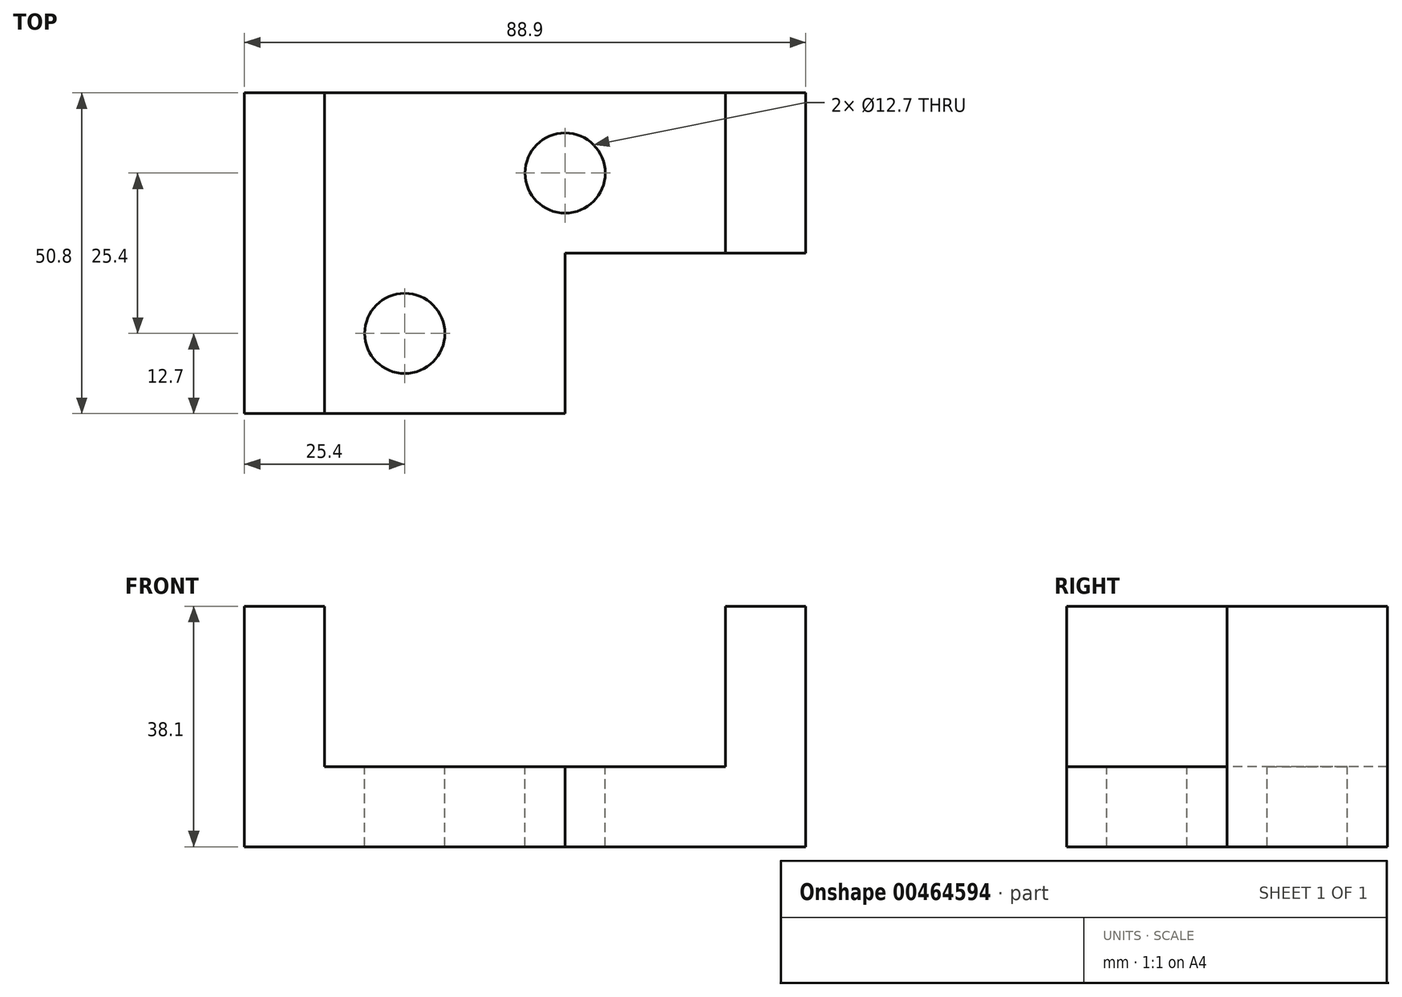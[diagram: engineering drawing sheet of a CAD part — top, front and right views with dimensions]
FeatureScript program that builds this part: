
annotation { "Feature Type Name" : "Feature", "Feature Type Description" : "" }
export const myFeature = defineFeature(function(context is Context, id is Id, definition is map)
    precondition{}
    {
        {
            var Q0;
            Q0=qCreatedBy(makeId("Front.planeOp"),FACE);
            var sketch = newSketch(context, id + "F0", { "sketchPlane" : qUnion([Q0])});
            skLineSegment(sketch, "E0.bottom", {"start": v(44.45, 19.05) * mm, "end": v(-44.45, 19.05) * mm});
            skLineSegment(sketch, "E0.top", {"start": v(44.45, -19.05) * mm, "end": v(-44.45, -19.05) * mm});
            skLineSegment(sketch, "E0.left", {"start": v(44.45, 19.05) * mm, "end": v(44.45, -19.05) * mm});
            skLineSegment(sketch, "E0.right", {"start": v(-44.45, 19.05) * mm, "end": v(-44.45, -19.05) * mm});
            skPoint(sketch, "E0.middle", {"position": v(0, 0) * mm});
            skSolve(sketch);
        }
        {
            var Q0;
            Q0=qSketchRegion(id+"F0",true);
            extrude(context, id + "F1", {"entities" : qUnion([Q0]), "depth" : 50.8 * mm});
        }
        {
            var Q0;
            Q0=makeQuery(id+"F1.opExtrude","CAP_FACE",FACE,{"disambiguationData":[OSD([sQuery(id+"F0.wireOp",EDGE,"E0.bottom"),sQuery(id+"F0.wireOp",EDGE,"E0.top"),sQuery(id+"F0.wireOp",EDGE,"E0.left"),sQuery(id+"F0.wireOp",EDGE,"E0.right")])],"isStart":false});
            var sketch = newSketch(context, id + "F2", { "sketchPlane" : qUnion([Q0])});
            skLineSegment(sketch, "E1", {"start": v(-44.45, 19.05) * mm, "end": v(-31.75, 19.05) * mm});
            skLineSegment(sketch, "E2", {"start": v(-31.75, -6.35) * mm, "end": v(-31.75, 19.05) * mm});
            skLineSegment(sketch, "E3", {"start": v(-31.75, -6.35) * mm, "end": v(31.75, -6.35) * mm});
            skLineSegment(sketch, "E4", {"start": v(31.75, -6.35) * mm, "end": v(31.75, 19.05) * mm});
            skLineSegment(sketch, "E5", {"start": v(31.75, 19.05) * mm, "end": v(44.45, 19.05) * mm});
            skSolve(sketch);
        }
        {
            var Q0;
            {var subQ0=sQuery(id+"F2.wireOp",EDGE,"E2");Q0=makeQuery(id+"F2.imprint","IMPRINT",FACE,{"disambiguationData":[TD([[makeQuery(id+"F2.imprint","IMPRINT",EDGE,{"derivedFrom":subQ0}),-1.0]])]});}
            extrude(context, id + "F3", {"entities" : qUnion([Q0]), "operationType" : NewBodyOperationType.REMOVE, "endBound" : BoundingType.THROUGH_ALL, "oppositeDirection" : true, "depth" : 25.4 * mm});
        }
        {
            var Q0;
            Q0=makeQuery(id+"F3.boolean.opBoolean","COPY",FACE,{"derivedFrom":makeQuery(id+"F3.opExtrude","SWEPT_FACE",FACE,{"disambiguationData":[OSD([sQuery(id+"F2.wireOp",EDGE,"E3")])]})});
            var sketch = newSketch(context, id + "F4", { "sketchPlane" : qUnion([Q0])});
            skPoint(sketch, "E6.startSnap0", {"position": v(6.35, -25.4) * mm});
            skLineSegment(sketch, "E7.bottom", {"start": v(6.35, -25.4) * mm, "end": v(31.75, -25.4) * mm});
            skLineSegment(sketch, "E7.top", {"start": v(6.35, -50.8) * mm, "end": v(31.75, -50.8) * mm});
            skLineSegment(sketch, "E7.left", {"start": v(6.35, -25.4) * mm, "end": v(6.35, -50.8) * mm});
            skLineSegment(sketch, "E7.right", {"start": v(31.75, -25.4) * mm, "end": v(31.75, -50.8) * mm});
            skSolve(sketch);
        }
        {
            var Q0;
            Q0=makeQuery(id+"F4.imprint","IMPRINT",FACE,{"disambiguationData":[TD([[makeQuery(id+"F4.imprint","IMPRINT",EDGE,{"derivedFrom":sQuery(id+"F4.wireOp",EDGE,"E7.bottom")}),-1.0]])]});
            extrude(context, id + "F5", {"entities" : qUnion([Q0]), "operationType" : NewBodyOperationType.REMOVE, "endBound" : BoundingType.THROUGH_ALL, "oppositeDirection" : true, "depth" : 25.4 * mm});
        }
        {
            var Q0;
            {var subQ1=sQuery(id+"F0.wireOp",EDGE,"E0.left");var subQ3=sQuery(id+"F0.wireOp",EDGE,"E0.bottom");Q0=makeQuery(id+"F3.boolean.opBoolean","SPLIT",FACE,{"disambiguationData":[TD([makeQuery(id+"F1.opExtrude","SWEPT_FACE",FACE,{"disambiguationData":[OSD([subQ1])]})])],"derivedFrom":makeQuery(id+"F1.opExtrude","SWEPT_FACE",FACE,{"disambiguationData":[OSD([subQ3])]})});}
            var sketch = newSketch(context, id + "F6", { "sketchPlane" : qUnion([Q0])});
            skLineSegment(sketch, "E8.bottom", {"start": v(31.75, -25.4) * mm, "end": v(44.45, -25.4) * mm});
            skLineSegment(sketch, "E8.top", {"start": v(31.75, -50.8) * mm, "end": v(44.45, -50.8) * mm});
            skLineSegment(sketch, "E8.left", {"start": v(31.75, -25.4) * mm, "end": v(31.75, -50.8) * mm});
            skLineSegment(sketch, "E8.right", {"start": v(44.45, -25.4) * mm, "end": v(44.45, -50.8) * mm});
            skSolve(sketch);
        }
        {
            var Q0;
            Q0=makeQuery(id+"F6.imprint","IMPRINT",FACE,{"disambiguationData":[TD([[makeQuery(id+"F6.imprint","IMPRINT",EDGE,{"derivedFrom":sQuery(id+"F6.wireOp",EDGE,"E8.bottom")}),-1.0]])]});
            extrude(context, id + "F7", {"entities" : qUnion([Q0]), "operationType" : NewBodyOperationType.REMOVE, "endBound" : BoundingType.THROUGH_ALL, "oppositeDirection" : true, "depth" : 25.4 * mm});
        }
        {
            var Q0;
            Q0=makeQuery(id+"F3.boolean.opBoolean","COPY",FACE,{"derivedFrom":makeQuery(id+"F3.opExtrude","SWEPT_FACE",FACE,{"disambiguationData":[OSD([sQuery(id+"F2.wireOp",EDGE,"E3")])]})});
            var sketch = newSketch(context, id + "F8", { "sketchPlane" : qUnion([Q0])});
            skCircle(sketch, "E9", {"center": v(6.35, -12.7) * mm, "radius": 6.35 * mm});
            skSolve(sketch);
        }
        {
            var Q0;
            Q0=makeQuery(id+"F8.imprint","IMPRINT",FACE,{"disambiguationData":[TD([[makeQuery(id+"F8.imprint","IMPRINT",EDGE,{"derivedFrom":sQuery(id+"F8.wireOp",EDGE,"E9")}),1.0]])]});
            extrude(context, id + "F9", {"entities" : qUnion([Q0]), "operationType" : NewBodyOperationType.REMOVE, "endBound" : BoundingType.THROUGH_ALL, "oppositeDirection" : true, "depth" : 25.4 * mm});
        }
        {
            var Q0;
            Q0=makeQuery(id+"F3.boolean.opBoolean","COPY",FACE,{"derivedFrom":makeQuery(id+"F3.opExtrude","SWEPT_FACE",FACE,{"disambiguationData":[OSD([sQuery(id+"F2.wireOp",EDGE,"E3")])]})});
            var sketch = newSketch(context, id + "F10", { "sketchPlane" : qUnion([Q0])});
            skLineSegment(sketch, "E10", {"start": v(6.35, -50.8) * mm, "end": v(-19.05, -50.8) * mm});
            skLineSegment(sketch, "E11", {"start": v(6.35, -25.4) * mm, "end": v(6.35, -38.1) * mm});
            skPoint(sketch, "E12", {"position": v(-19.05, -38.1) * mm});
            skCircle(sketch, "E13", {"center": v(-19.05, -38.1) * mm, "radius": 6.35 * mm});
            skSolve(sketch);
        }
        {
            var Q0;
            Q0=makeQuery(id+"F10.imprint","IMPRINT",FACE,{"disambiguationData":[TD([[makeQuery(id+"F10.imprint","IMPRINT",EDGE,{"derivedFrom":sQuery(id+"F10.wireOp",EDGE,"E13")}),1.0]])]});
            extrude(context, id + "F11", {"entities" : qUnion([Q0]), "operationType" : NewBodyOperationType.REMOVE, "endBound" : BoundingType.THROUGH_ALL, "oppositeDirection" : true, "depth" : 25.4 * mm});
        }
    });
